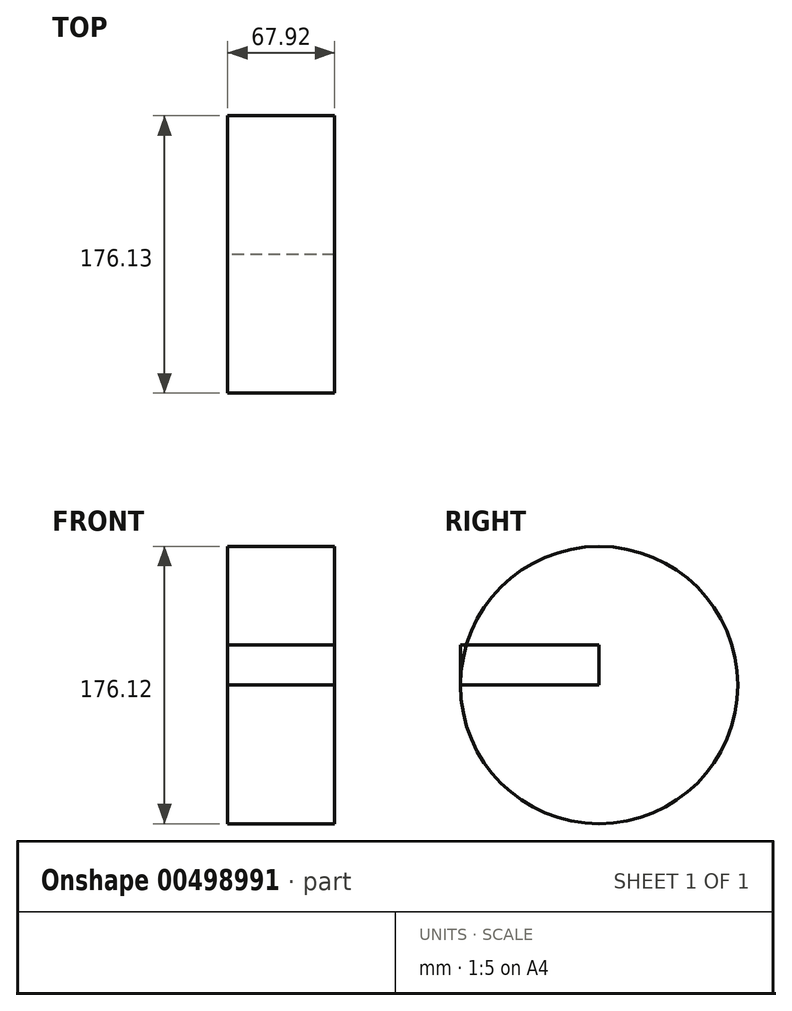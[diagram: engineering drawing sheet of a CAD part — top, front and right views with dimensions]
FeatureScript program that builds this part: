
annotation { "Feature Type Name" : "Feature", "Feature Type Description" : "" }
export const myFeature = defineFeature(function(context is Context, id is Id, definition is map)
    precondition{}
    {
        {
            var Q0;
            Q0=qCreatedBy(makeId("Top.planeOp"),FACE);
            var sketch = newSketch(context, id + "F0", { "sketchPlane" : qUnion([Q0])});
            skLineSegment(sketch, "E0.bottom", {"start": v(33.96, 44.03) * mm, "end": v(-33.96, 44.03) * mm});
            skLineSegment(sketch, "E0.top", {"start": v(33.96, -44.03) * mm, "end": v(-33.96, -44.03) * mm});
            skLineSegment(sketch, "E0.left", {"start": v(33.96, 44.03) * mm, "end": v(33.96, -44.03) * mm});
            skLineSegment(sketch, "E0.right", {"start": v(-33.96, 44.03) * mm, "end": v(-33.96, -44.03) * mm});
            skPoint(sketch, "E0.middle", {"position": v(0, 0) * mm});
            skSolve(sketch);
        }
        {
            var Q0;
            Q0=makeQuery(id+"F0.imprint","IMPRINT",FACE,{"disambiguationData":[TD([[makeQuery(id+"F0.imprint","IMPRINT",EDGE,{"derivedFrom":sQuery(id+"F0.wireOp",EDGE,"E0.bottom")}),1.0]])]});
            var Q1;
            Q1=sQuery(id+"F0.wireOp",EDGE,"E0.bottom");
            revolve(context, id + "F1", {"entities" : qUnion([Q0]), "axis" : qUnion([Q1]), "revolveType" : RevolveType.FULL});
        }
        {
            var Q0;
            Q0=makeQuery(id+"F0.imprint","IMPRINT",FACE,{"disambiguationData":[TD([[makeQuery(id+"F0.imprint","IMPRINT",EDGE,{"derivedFrom":sQuery(id+"F0.wireOp",EDGE,"E0.bottom")}),1.0]])]});
            extrude(context, id + "F2", {"entities" : qUnion([Q0]), "depth" : 25.4 * mm});
        }
    });
